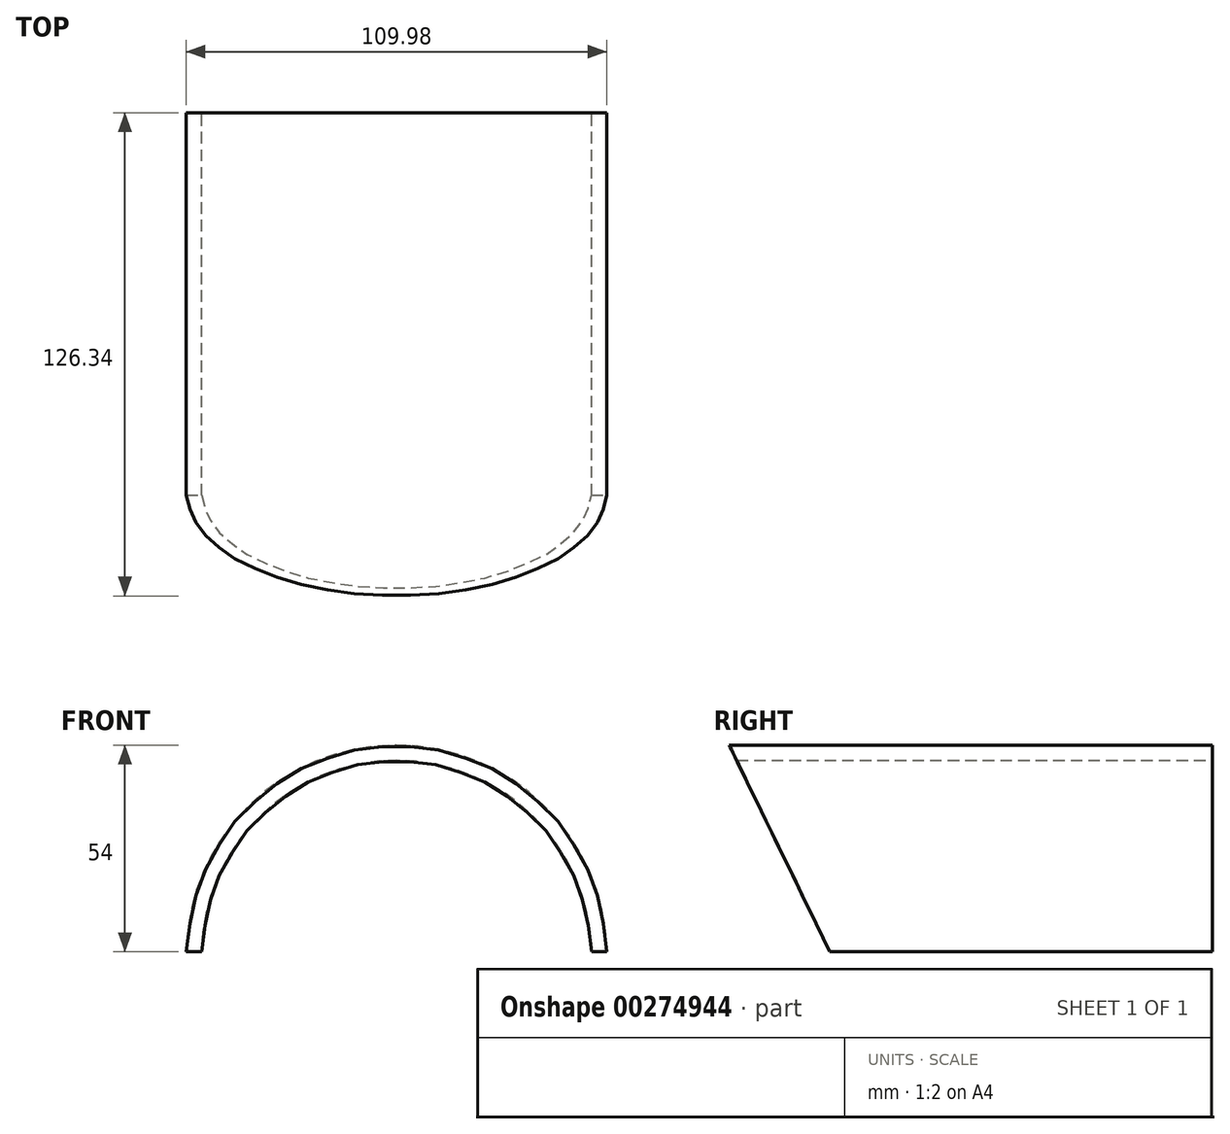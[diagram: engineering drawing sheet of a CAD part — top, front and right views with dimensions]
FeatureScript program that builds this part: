
annotation { "Feature Type Name" : "Feature", "Feature Type Description" : "" }
export const myFeature = defineFeature(function(context is Context, id is Id, definition is map)
    precondition{}
    {
        {
            var Q0;
            Q0=qCreatedBy(makeId("Front.planeOp"),FACE);
            var sketch = newSketch(context, id + "F0", { "sketchPlane" : qUnion([Q0])});
            skArc(sketch, "E0", {"start": v(55, 1) * mm, "mid": v(0, 55) * mm, "end": v(-55, 1) * mm});
            skArc(sketch, "E1", {"start": v(51, 1) * mm, "mid": v(0, 51) * mm, "end": v(-51, 1) * mm});
            skLineSegment(sketch, "E2", {"start": v(-55, 1) * mm, "end": v(-51, 1) * mm});
            skLineSegment(sketch, "E3.trimOffspring", {"start": v(51, 1) * mm, "end": v(55, 1) * mm});
            skSolve(sketch);
        }
        {
            var Q0;
            Q0=makeQuery(id+"F0.imprint","IMPRINT",FACE,{"disambiguationData":[TD([[makeQuery(id+"F0.imprint","IMPRINT",EDGE,{"derivedFrom":sQuery(id+"F0.wireOp",EDGE,"E0")}),1.0]])]});
            extrude(context, id + "F1", {"entities" : qUnion([Q0]), "depth" : 127 * mm});
        }
        {
            var Q0;
            Q0=qCreatedBy(makeId("Front.planeOp"),FACE);
            cPlane(context, id + "F2", {"entities" : qUnion([Q0]), "cplaneType" : CPlaneType.OFFSET, "offset" : 100 * mm, "width" : 150 * mm, "height" : 150 * mm});
        }
        {
            var Q0;
            Q0=qCreatedBy(id+"F2.planeOp",FACE);
            var sketch = newSketch(context, id + "F3", { "sketchPlane" : qUnion([Q0])});
            skLineSegment(sketch, "E4.0", {"start": v(51, 1) * mm, "end": v(55, 1) * mm});
            skSolve(sketch);
        }
        {
            var Q0;
            Q0=sQuery(id+"F3.wireOp",EDGE,"E4.0");
            cPlane(context, id + "F4", {"entities" : qUnion([Q0]), "cplaneType" : CPlaneType.LINE_ANGLE, "offset" : 25 * mm, "angle" : 26 * degree, "width" : 150 * mm, "height" : 150 * mm});
        }
        {
            var Q0;
            Q0=makeQuery(id+"F1.opExtrude","CAP_FACE",FACE,{"disambiguationData":[OSD([sQuery(id+"F0.wireOp",EDGE,"E0"),sQuery(id+"F0.wireOp",EDGE,"E1"),sQuery(id+"F0.wireOp",EDGE,"E2"),sQuery(id+"F0.wireOp",EDGE,"E3.trimOffspring")])],"isStart":false});
            var Q1;
            Q1=qCreatedBy(id+"F4.planeOp",FACE);
            extrude(context, id + "F5", {"entities" : qUnion([Q0]), "operationType" : NewBodyOperationType.REMOVE, "endBound" : BoundingType.UP_TO_SURFACE, "oppositeDirection" : true, "endBoundEntityFace" : qUnion([Q1]), "depth" : 25 * mm});
        }
    });
